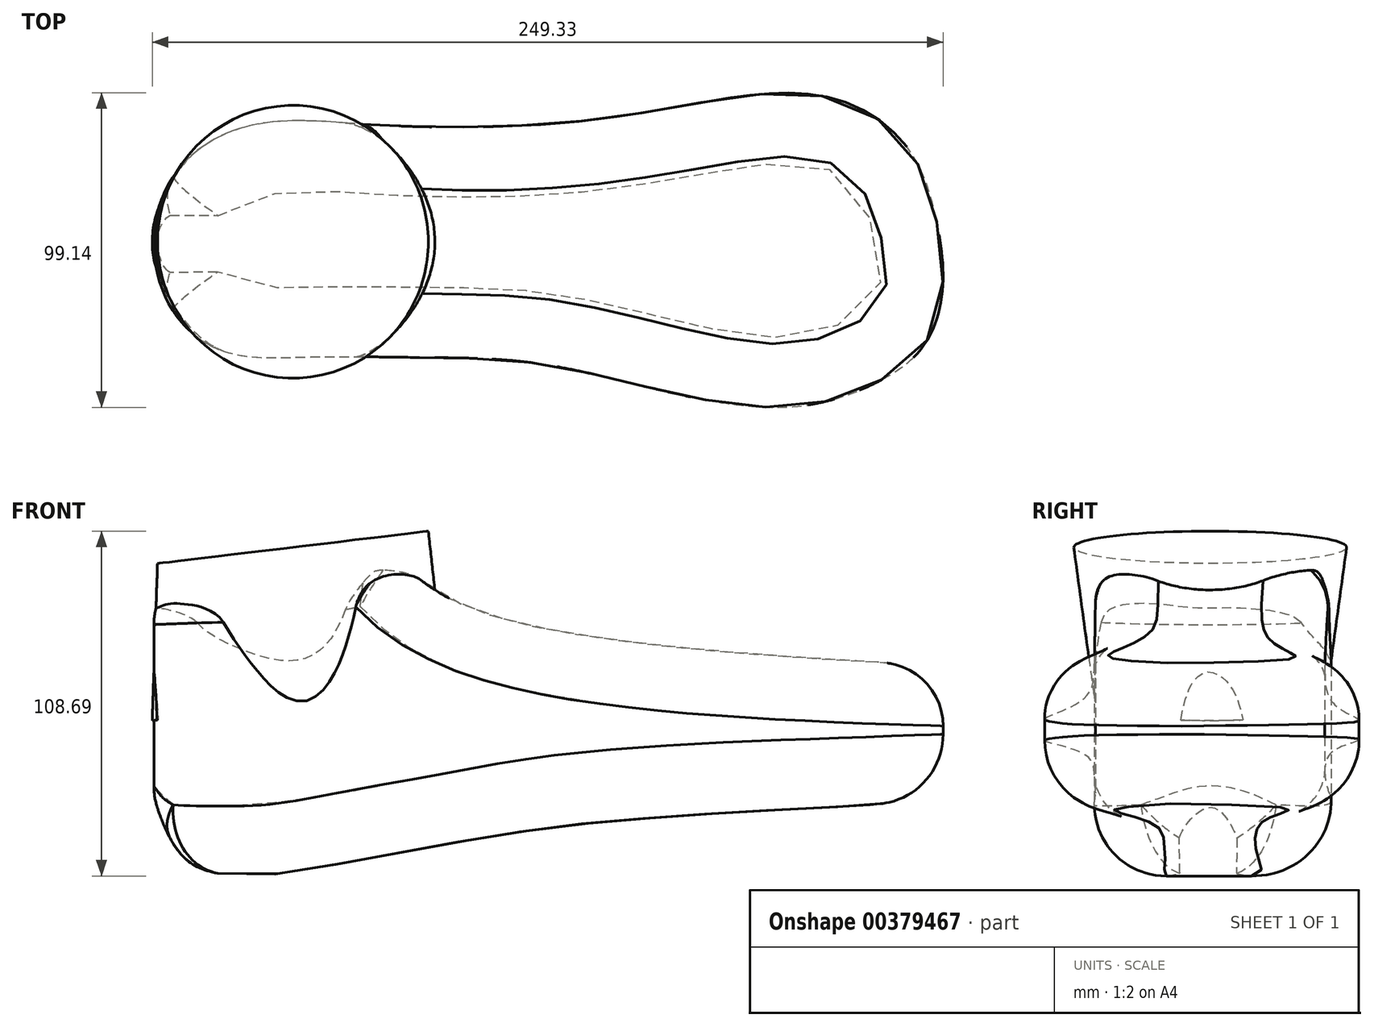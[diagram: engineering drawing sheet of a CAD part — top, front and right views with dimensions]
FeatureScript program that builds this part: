
annotation { "Feature Type Name" : "Feature", "Feature Type Description" : "" }
export const myFeature = defineFeature(function(context is Context, id is Id, definition is map)
    precondition{}
    {
        {
            var Q0;
            Q0=qCreatedBy(makeId("Top.planeOp"),FACE);
            cPlane(context, id + "F0", {"entities" : qUnion([Q0]), "cplaneType" : CPlaneType.OFFSET, "offset" : 10 * mm, "oppositeDirection" : true, "width" : 150 * mm, "height" : 150 * mm});
        }
        {
            var Q0;
            Q0=qCreatedBy(makeId("Front.planeOp"),FACE);
            var sketch = newSketch(context, id + "F1", { "sketchPlane" : qUnion([Q0])});
            skLineSegment(sketch, "E0", {"start": v(-126.2, 34.59) * mm, "end": v(0, 49.64) * mm, "construction": true});
            skSolve(sketch);
        }
        {
            var Q0;
            Q0=qCreatedBy(makeId("Right.planeOp"),FACE);
            var sketch = newSketch(context, id + "F2", { "sketchPlane" : qUnion([Q0])});
            skLineSegment(sketch, "E1.0", {"start": v(0, 34.59) * mm, "end": v(0, 49.64) * mm, "construction": true});
            skLineSegment(sketch, "E2", {"start": v(0, 49.64) * mm, "end": v(78.18, 49.64) * mm, "construction": true});
            skSolve(sketch);
        }
        {
            var Q0;
            Q0=sQuery(id+"F2.wireOp",VERTEX,"E2.end");
            var Q1;
            Q1=sQuery(id+"F2.wireOp",VERTEX,"E2.start");
            var Q2;
            Q2=sQuery(id+"F1.wireOp",VERTEX,"E0.start");
            cPlane(context, id + "F3", {"entities" : qUnion([Q0, Q1, Q2]), "cplaneType" : CPlaneType.THREE_POINT, "offset" : 25 * mm, "width" : 150 * mm, "height" : 150 * mm});
        }
        {
            var Q0;
            Q0=qCreatedBy(id+"F0.planeOp",FACE);
            cPlane(context, id + "F4", {"entities" : qUnion([Q0]), "cplaneType" : CPlaneType.OFFSET, "offset" : 70 * mm, "width" : 150 * mm, "height" : 150 * mm});
        }
        {
            var Q0;
            Q0=qCreatedBy(id+"F4.planeOp",FACE);
            var sketch = newSketch(context, id + "F5", { "sketchPlane" : qUnion([Q0])});
            skLineSegment(sketch, "E3.bottom", {"start": v(178, 87.04) * mm, "end": v(-168.77, 87.04) * mm});
            skLineSegment(sketch, "E3.top", {"start": v(178, -71.84) * mm, "end": v(-168.77, -71.84) * mm});
            skLineSegment(sketch, "E3.left", {"start": v(178, 87.04) * mm, "end": v(178, -71.84) * mm});
            skLineSegment(sketch, "E3.right", {"start": v(-168.77, 87.04) * mm, "end": v(-168.77, -71.84) * mm});
            skFitSpline(sketch, "E4", {"points": [v(105.9, -43.98) * mm, v(120.56, -32.07) * mm, v(126.05, -14.96) * mm, v(124.8, 3.26) * mm, v(117.36, 26.09) * mm, v(100.82, 41.65) * mm, v(80.47, 46.85) * mm, v(55.8, 44.85) * mm, v(19.69, 38.96) * mm, v(-18.8, 36.21) * mm, v(-55.07, 36.97) * mm, v(-78, 38.15) * mm, v(-97.37, 35.08) * mm, v(-113.72, 24.15) * mm, v(-122.11, 6.16) * mm, v(-120.89, -12.02) * mm, v(-115.3, -23.54) * mm, v(-105.57, -32.28) * mm, v(-91.66, -36.26) * mm, v(-71.4, -36.26) * mm, v(-39.4, -36.46) * mm, v(-2.44, -38.24) * mm, v(40.03, -47.42) * mm, v(79, -51.98) * mm, v(105.9, -43.98) * mm]});
            skSolve(sketch);
        }
        {
            var Q0;
            Q0=qCreatedBy(makeId("Front.planeOp"),FACE);
            var sketch = newSketch(context, id + "F6", { "sketchPlane" : qUnion([Q0])});
            skFitSpline(sketch, "E5", {"points": [v(-119.13, 38.44) * mm, v(-119.13, 33.94) * mm, v(-120.9, 4.27) * mm, v(-123.57, -25.48) * mm, v(-120.92, -39.45) * mm, v(-113.66, -52.87) * mm, v(-104.36, -58.06) * mm, v(-92.75, -59.32) * mm, v(-77.53, -57.75) * mm, v(-27.63, -48.8) * mm, v(12.86, -42.84) * mm, v(69.82, -38.75) * mm, v(100.89, -37.03) * mm, v(116.9, -34.52) * mm, v(127.68, -28.43) * mm, v(131.34, -21.72) * mm, v(132.41, -11.5) * mm, v(130.12, -3.1) * mm, v(121.42, 4.53) * mm, v(108.1, 7.85) * mm, v(96.18, 8.64) * mm, v(56.48, 11.46) * mm, v(17.18, 15.9) * mm, v(-25.8, 26.38) * mm, v(-43.72, 38.7) * mm, v(-47, 43.48) * mm, v(-49.25, 47.59) * mm, v(-60.65, 45.69) * mm, v(-113.57, 39.24) * mm, v(-119.13, 38.44) * mm]});
            skSolve(sketch);
        }
        {
            var Q0;
            Q0=qSketchRegion(id+"F6",true);
            extrude(context, id + "F7", {"entities" : qUnion([Q0]), "depth" : 140 * mm, "symmetric" : true});
        }
        {
            var Q0;
            Q0=makeQuery(id+"F5.imprint","IMPRINT",FACE,{"disambiguationData":[TD([[makeQuery(id+"F5.imprint","IMPRINT",EDGE,{"derivedFrom":sQuery(id+"F5.wireOp",EDGE,"E3.bottom")}),1.0]])]});
            extrude(context, id + "F8", {"entities" : qUnion([Q0]), "operationType" : NewBodyOperationType.REMOVE, "oppositeDirection" : true, "depth" : 130 * mm});
        }
        {
            var Q0;
            Q0=makeQuery(id+"F8.boolean.opBoolean","INTERSECT",EDGE,{"disambiguationData":[OD(1.0)],"derivedFrom":[makeQuery(id+"F7.opExtrude","SWEPT_FACE",FACE,{"disambiguationData":[OSD([sQuery(id+"F6.wireOp",EDGE,"E5")])]}),makeQuery(id+"F8.opExtrude","SWEPT_FACE",FACE,{"disambiguationData":[OSD([sQuery(id+"F5.wireOp",EDGE,"E4")])]})]});
            fillet(context, id + "F9", {"entities" : qUnion([Q0]), "radius" : 20 * mm, "allowEdgeOverflow" : false});
        }
        {
            var Q0;
            Q0=makeQuery(id+"F8.boolean.opBoolean","INTERSECT",EDGE,{"disambiguationData":[OD(0.0)],"derivedFrom":[makeQuery(id+"F7.opExtrude","SWEPT_FACE",FACE,{"disambiguationData":[OSD([sQuery(id+"F6.wireOp",EDGE,"E5")])]}),makeQuery(id+"F8.opExtrude","SWEPT_FACE",FACE,{"disambiguationData":[OSD([sQuery(id+"F5.wireOp",EDGE,"E4")])]})]});
            fillet(context, id + "F10", {"entities" : qUnion([Q0]), "radius" : 22 * mm, "tangentPropagation" : true, "allowEdgeOverflow" : false});
        }
        {
            var Q0;
            Q0=qCreatedBy(id+"F3.planeOp",FACE);
            var sketch = newSketch(context, id + "F11", { "sketchPlane" : qUnion([Q0])});
            skLineSegment(sketch, "E6.bottom", {"start": v(-167.37, -58.49) * mm, "end": v(31.87, -58.49) * mm});
            skLineSegment(sketch, "E6.top", {"start": v(-167.37, 81.96) * mm, "end": v(31.87, 81.96) * mm});
            skLineSegment(sketch, "E6.left", {"start": v(-167.37, -58.49) * mm, "end": v(-167.37, 81.96) * mm});
            skLineSegment(sketch, "E6.right", {"start": v(31.87, -58.49) * mm, "end": v(31.87, 81.96) * mm});
            skSolve(sketch);
        }
        {
            var Q0;
            Q0=makeQuery(id+"F11.imprint","IMPRINT",FACE,{"disambiguationData":[TD([[makeQuery(id+"F11.imprint","IMPRINT",EDGE,{"derivedFrom":sQuery(id+"F11.wireOp",EDGE,"E6.bottom")}),1.0]])]});
            extrude(context, id + "F12", {"entities" : qUnion([Q0]), "operationType" : NewBodyOperationType.REMOVE, "depth" : 10 * mm, "symmetric" : true});
        }
        {
            var Q0;
            Q0=qCreatedBy(id+"F3.planeOp",FACE);
            cPlane(context, id + "F13", {"entities" : qUnion([Q0]), "cplaneType" : CPlaneType.OFFSET, "offset" : 96 * mm, "oppositeDirection" : true, "width" : 150 * mm, "height" : 150 * mm});
        }
        {
            var Q0;
            Q0=qCreatedBy(id+"F13.planeOp",FACE);
            cPlane(context, id + "F14", {"entities" : qUnion([Q0]), "cplaneType" : CPlaneType.OFFSET, "offset" : 100 * mm, "width" : 150 * mm, "height" : 150 * mm});
        }
        {
            var Q0;
            Q0=qCreatedBy(id+"F14.planeOp",FACE);
            var sketch = newSketch(context, id + "F15", { "sketchPlane" : qUnion([Q0])});
            skCircle(sketch, "E7", {"center": v(-72.94, 0) * mm, "radius": 43 * mm});
            skSolve(sketch);
        }
        {
            var Q0;
            Q0=qCreatedBy(id+"F3.planeOp",FACE);
            cPlane(context, id + "F16", {"entities" : qUnion([Q0]), "cplaneType" : CPlaneType.OFFSET, "offset" : 45 * mm, "oppositeDirection" : true, "width" : 150 * mm, "height" : 150 * mm});
        }
        {
            var Q0;
            Q0=qCreatedBy(id+"F16.planeOp",FACE);
            var sketch = newSketch(context, id + "F17", { "sketchPlane" : qUnion([Q0])});
            skEllipse(sketch, "E8", {"center": v(-76.91, 0) * mm, "majorRadius": 46.54 * mm, "minorRadius": 36.31 * mm, "majorAxis": v(1, 0)});
            skSolve(sketch);
        }
        {
            var Q1;
            Q1=qSketchRegion(id+"F15",true);
            var Q2;
            Q2=qSketchRegion(id+"F17",true);
            loft(context, id + "F18", {"operationType" : NewBodyOperationType.ADD, "sheetProfilesArray" : [{ "sheetProfileEntities" : qUnion([Q1]) }, { "sheetProfileEntities" : qUnion([Q2]) }]});
        }
    });
